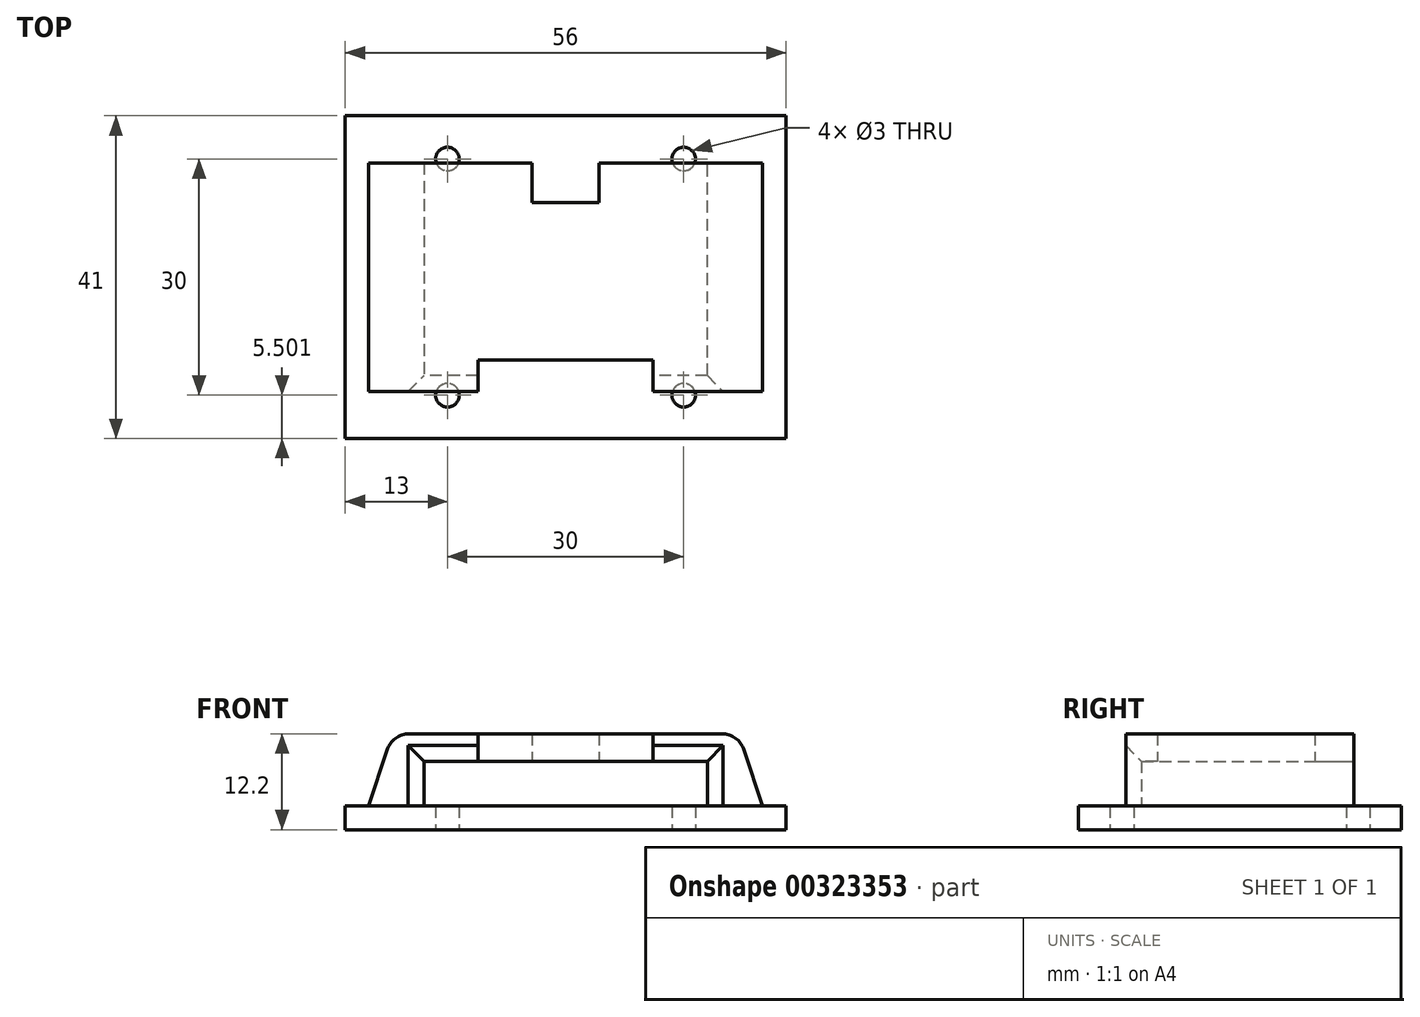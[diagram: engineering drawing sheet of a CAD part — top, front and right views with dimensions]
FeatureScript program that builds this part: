
annotation { "Feature Type Name" : "Feature", "Feature Type Description" : "" }
export const myFeature = defineFeature(function(context is Context, id is Id, definition is map)
    precondition{}
    {
        {
            var Q0;
            Q0=qCreatedBy(makeId("Top.planeOp"),FACE);
            var sketch = newSketch(context, id + "F0", { "sketchPlane" : qUnion([Q0])});
            skLineSegment(sketch, "E0", {"start": v(-18, 12.15) * mm, "end": v(-4.25, 12.15) * mm});
            skLineSegment(sketch, "E1", {"start": v(-4.25, 12.15) * mm, "end": v(-4.25, 7.15) * mm});
            skLineSegment(sketch, "E2", {"start": v(-4.25, 7.15) * mm, "end": v(4.25, 7.15) * mm});
            skLineSegment(sketch, "E3", {"start": v(4.25, 7.15) * mm, "end": v(4.25, 12.15) * mm});
            skLineSegment(sketch, "E4", {"start": v(4.25, 12.15) * mm, "end": v(18, 12.15) * mm});
            skLineSegment(sketch, "E5", {"start": v(18, 12.15) * mm, "end": v(18, -16.85) * mm});
            skLineSegment(sketch, "E6", {"start": v(18, -16.85) * mm, "end": v(11.12, -16.85) * mm});
            skLineSegment(sketch, "E7", {"start": v(11.12, -16.85) * mm, "end": v(11.12, -12.85) * mm});
            skLineSegment(sketch, "E8", {"start": v(11.12, -12.85) * mm, "end": v(-11.12, -12.85) * mm});
            skLineSegment(sketch, "E9", {"start": v(-11.12, -12.85) * mm, "end": v(-11.12, -16.85) * mm});
            skLineSegment(sketch, "E10", {"start": v(-11.12, -16.85) * mm, "end": v(-18, -16.85) * mm});
            skLineSegment(sketch, "E11", {"start": v(-18, -16.85) * mm, "end": v(-18, 12.15) * mm});
            skSolve(sketch);
        }
        {
            var Q0;
            Q0=qSketchRegion(id+"F0",true);
            extrude(context, id + "F1", {"entities" : qUnion([Q0]), "depth" : 3.5 * mm});
        }
        {
            var Q0;
            Q0=makeQuery(id+"F1.opExtrude","SWEPT_FACE",FACE,{"disambiguationData":[OSD([sQuery(id+"F0.wireOp",EDGE,"E11")])]});
            var sketch = newSketch(context, id + "F2", { "sketchPlane" : qUnion([Q0])});
            skLineSegment(sketch, "E12.bottom", {"start": v(-12.15, 3.5) * mm, "end": v(16.85, 3.5) * mm});
            skLineSegment(sketch, "E12.top", {"start": v(-12.15, -5.7) * mm, "end": v(16.85, -5.7) * mm});
            skLineSegment(sketch, "E12.left", {"start": v(-12.15, 3.5) * mm, "end": v(-12.15, -5.7) * mm});
            skLineSegment(sketch, "E12.right", {"start": v(16.85, 3.5) * mm, "end": v(16.85, -5.7) * mm});
            skSolve(sketch);
        }
        {
            var Q0;
            Q0=qSketchRegion(id+"F2",true);
            extrude(context, id + "F3", {"entities" : qUnion([Q0]), "operationType" : NewBodyOperationType.ADD, "depth" : 4 * mm});
        }
        {
            var Q0;
            Q0=makeQuery(id+"F1.opExtrude","SWEPT_FACE",FACE,{"disambiguationData":[OSD([sQuery(id+"F0.wireOp",EDGE,"E5")])]});
            var sketch = newSketch(context, id + "F4", { "sketchPlane" : qUnion([Q0])});
            skLineSegment(sketch, "E13.bottom", {"start": v(-16.85, 3.5) * mm, "end": v(12.15, 3.5) * mm});
            skLineSegment(sketch, "E13.top", {"start": v(-16.85, -5.7) * mm, "end": v(12.15, -5.7) * mm});
            skLineSegment(sketch, "E13.left", {"start": v(-16.85, 3.5) * mm, "end": v(-16.85, -5.7) * mm});
            skLineSegment(sketch, "E13.right", {"start": v(12.15, 3.5) * mm, "end": v(12.15, -5.7) * mm});
            skSolve(sketch);
        }
        {
            var Q0;
            Q0=qSketchRegion(id+"F4",true);
            extrude(context, id + "F5", {"entities" : qUnion([Q0]), "operationType" : NewBodyOperationType.ADD, "depth" : 4 * mm});
        }
        {
            var Q0;
            Q0=makeQuery(id+"F1.opExtrude","CAP_EDGE",EDGE,{"disambiguationData":[OSD([sQuery(id+"F0.wireOp",EDGE,"E10")])],"isStart":true});
            var Q1;
            Q1=makeQuery(id+"F1.opExtrude","CAP_EDGE",EDGE,{"disambiguationData":[OSD([sQuery(id+"F0.wireOp",EDGE,"E6")])],"isStart":true});
            chamfer(context, id + "F6", {"entities" : qUnion([Q0, Q1]), "width" : 2 * mm, "tangentPropagation" : true});
        }
        {
            var Q0;
            Q0=makeQuery(id+"F5.opExtrude","SWEPT_FACE",FACE,{"disambiguationData":[OSD([sQuery(id+"F4.wireOp",EDGE,"E13.top")])]});
            var sketch = newSketch(context, id + "F7", { "sketchPlane" : qUnion([Q0])});
            skLineSegment(sketch, "E14.bottom", {"start": v(22, -5.15) * mm, "end": v(18, -5.15) * mm});
            skLineSegment(sketch, "E14.top", {"start": v(22, 9.85) * mm, "end": v(18, 9.85) * mm});
            skLineSegment(sketch, "E14.left", {"start": v(22, -5.15) * mm, "end": v(22, 9.85) * mm});
            skLineSegment(sketch, "E14.right", {"start": v(18, -5.15) * mm, "end": v(18, 9.85) * mm});
            skLineSegment(sketch, "E15", {"start": v(41.9, 2.35) * mm, "end": v(-44.93, 2.35) * mm, "construction": true});
            skLineSegment(sketch, "E16.bottom", {"start": v(-22, -5.15) * mm, "end": v(-18, -5.15) * mm});
            skLineSegment(sketch, "E16.top", {"start": v(-22, 9.85) * mm, "end": v(-18, 9.85) * mm});
            skLineSegment(sketch, "E16.left", {"start": v(-22, -5.15) * mm, "end": v(-22, 9.85) * mm});
            skLineSegment(sketch, "E16.right", {"start": v(-18, -5.15) * mm, "end": v(-18, 9.85) * mm});
            skSolve(sketch);
        }
        {
            var Q0;
            Q0=qSketchRegion(id+"F7",true);
            extrude(context, id + "F8", {"entities" : qUnion([Q0]), "operationType" : NewBodyOperationType.ADD, "depth" : 3 * mm});
        }
        {
            var Q0;
            Q0=makeQuery(id+"F5.opExtrude","CAP_EDGE",EDGE,{"disambiguationData":[OSD([sQuery(id+"F4.wireOp",EDGE,"E13.left")])],"isStart":true});
            var Q1;
            Q1=makeQuery(id+"F3.opExtrude","CAP_EDGE",EDGE,{"disambiguationData":[OSD([sQuery(id+"F2.wireOp",EDGE,"E12.right")])],"isStart":true});
            chamfer(context, id + "F9", {"entities" : qUnion([Q0, Q1]), "width" : 2 * mm, "tangentPropagation" : true});
        }
        {
            var Q0;
            Q0=makeQuery(id+"F3.boolean.opBoolean","MERGE",FACE,{"derivedFrom":[makeQuery(id+"F1.opExtrude","SWEPT_FACE",FACE,{"disambiguationData":[OSD([sQuery(id+"F0.wireOp",EDGE,"E0")])]}),makeQuery(id+"F3.opExtrude","SWEPT_FACE",FACE,{"disambiguationData":[OSD([sQuery(id+"F2.wireOp",EDGE,"E12.left")])]})]});
            var sketch = newSketch(context, id + "F10", { "sketchPlane" : qUnion([Q0])});
            skLineSegment(sketch, "E17", {"start": v(22, 3.5) * mm, "end": v(22, -5.7) * mm});
            skLineSegment(sketch, "E18", {"start": v(22, -5.7) * mm, "end": v(25, -5.7) * mm});
            skLineSegment(sketch, "E19", {"start": v(25, -5.7) * mm, "end": v(22, 3.5) * mm});
            skLineSegment(sketch, "E20", {"start": v(0, 10.19) * mm, "end": v(0, -17.52) * mm, "construction": true});
            skLineSegment(sketch, "E21.MirrorCS", {"start": v(-22, 3.5) * mm, "end": v(-22, -5.7) * mm});
            skLineSegment(sketch, "E22.MirrorCS", {"start": v(-22, -5.7) * mm, "end": v(-25, -5.7) * mm});
            skLineSegment(sketch, "E23.MirrorCS", {"start": v(-25, -5.7) * mm, "end": v(-22, 3.5) * mm});
            skSolve(sketch);
        }
        {
            var Q0;
            Q0=qSketchRegion(id+"F10",true);
            var Q1;
            Q1=makeQuery(id+"F3.boolean.opBoolean","MERGE",FACE,{"derivedFrom":[makeQuery(id+"F1.opExtrude","SWEPT_FACE",FACE,{"disambiguationData":[OSD([sQuery(id+"F0.wireOp",EDGE,"E10")])]}),makeQuery(id+"F3.opExtrude","SWEPT_FACE",FACE,{"disambiguationData":[OSD([sQuery(id+"F2.wireOp",EDGE,"E12.right")])]})]});
            extrude(context, id + "F11", {"entities" : qUnion([Q0]), "operationType" : NewBodyOperationType.ADD, "endBound" : BoundingType.UP_TO_SURFACE, "oppositeDirection" : true, "endBoundEntityFace" : qUnion([Q1]), "depth" : 25 * mm});
        }
        {
            var Q0;
            {var subQ0=sQuery(id+"F2.wireOp",EDGE,"E12.bottom");Q0=makeQuery(id+"F11.boolean.opBoolean","MERGE",EDGE,{"derivedFrom":[makeQuery(id+"F3.opExtrude","CAP_EDGE",EDGE,{"disambiguationData":[OSD([subQ0])],"isStart":false}),makeQuery(id+"F11.opExtrude","SWEPT_EDGE",EDGE,{"disambiguationData":[OSD([sQuery(id+"F0.wireOp",EDGE,"E0"),subQ0,sQuery(id+"F2.wireOp",EDGE,"E12.left"),sQuery(id+"F10.wireOp",EDGE,"E17"),sQuery(id+"F10.wireOp",EDGE,"E19")])]})]});}
            var Q1;
            Q1=makeQuery(id+"F11.boolean.opBoolean","MERGE",EDGE,{"derivedFrom":[makeQuery(id+"F5.opExtrude","CAP_EDGE",EDGE,{"disambiguationData":[OSD([sQuery(id+"F4.wireOp",EDGE,"E13.bottom")])],"isStart":false}),makeQuery(id+"F11.opExtrude","SWEPT_EDGE",EDGE,{"disambiguationData":[OSD([sQuery(id+"F10.wireOp",EDGE,"E21.MirrorCS"),sQuery(id+"F10.wireOp",EDGE,"E23.MirrorCS")])]})]});
            fillet(context, id + "F12", {"entities" : qUnion([Q0, Q1]), "radius" : 3 * mm, "tangentPropagation" : true, "allowEdgeOverflow" : false});
        }
        {
            var Q0;
            {var subQ2=sQuery(id+"F4.wireOp",EDGE,"E13.top");var subQ8=makeQuery(id+"F5.opExtrude","SWEPT_FACE",FACE,{"disambiguationData":[OSD([subQ2])]});Q0=makeQuery(id+"F11.boolean.opBoolean","MERGE",FACE,{"derivedFrom":[makeQuery(id+"F8.boolean.opBoolean","SPLIT",FACE,{"disambiguationData":[TD([makeQuery(id+"F1.opExtrude","SWEPT_FACE",FACE,{"disambiguationData":[OSD([sQuery(id+"F0.wireOp",EDGE,"E4")])]})])],"derivedFrom":subQ8}),makeQuery(id+"F8.boolean.opBoolean","SPLIT",FACE,{"disambiguationData":[TD([makeQuery(id+"F1.opExtrude","SWEPT_FACE",FACE,{"disambiguationData":[OSD([sQuery(id+"F0.wireOp",EDGE,"E6")])]})])],"derivedFrom":subQ8}),makeQuery(id+"F11.opExtrude","SWEPT_FACE",FACE,{"disambiguationData":[OSD([sQuery(id+"F10.wireOp",EDGE,"E22.MirrorCS")])]})]});}
            var sketch = newSketch(context, id + "F13", { "sketchPlane" : qUnion([Q0])});
            skLineSegment(sketch, "E24.bottom", {"start": v(-28, 22.85) * mm, "end": v(28, 22.85) * mm});
            skLineSegment(sketch, "E24.top", {"start": v(-28, -18.15) * mm, "end": v(28, -18.15) * mm});
            skLineSegment(sketch, "E24.left", {"start": v(-28, 22.85) * mm, "end": v(-28, -18.15) * mm});
            skLineSegment(sketch, "E24.right", {"start": v(28, 22.85) * mm, "end": v(28, -18.15) * mm});
            skSolve(sketch);
        }
        {
            var Q0;
            Q0 = qSketchRegion(id + "F13", true);
            var Q1;
            Q1=makeQuery(id+"F8.opExtrude","CAP_FACE",FACE,{"disambiguationData":[OSD([sQuery(id+"F7.wireOp",EDGE,"E16.bottom"),sQuery(id+"F7.wireOp",EDGE,"E16.top"),sQuery(id+"F7.wireOp",EDGE,"E16.left"),sQuery(id+"F7.wireOp",EDGE,"E16.right")])],"isStart":false});
            extrude(context, id + "F14", {"entities" : qUnion([Q0]), "operationType" : NewBodyOperationType.ADD, "endBound" : BoundingType.UP_TO_SURFACE, "depth" : 25 * mm, "endBoundEntityFace" : qUnion([Q1]), "offsetDistance" : 25 * mm});
        }
        {
            var Q0;
            {var subQ0=sQuery(id+"F7.wireOp",EDGE,"E16.right");var subQ1=sQuery(id+"F7.wireOp",EDGE,"E16.left");var subQ2=sQuery(id+"F7.wireOp",EDGE,"E16.top");var subQ3=sQuery(id+"F7.wireOp",EDGE,"E16.bottom");Q0=makeQuery(id+"F14.boolean.opBoolean","MERGE",FACE,{"derivedFrom":[makeQuery(id+"F8.opExtrude","CAP_FACE",FACE,{"disambiguationData":[OSD([sQuery(id+"F7.wireOp",EDGE,"E14.bottom"),sQuery(id+"F7.wireOp",EDGE,"E14.top"),sQuery(id+"F7.wireOp",EDGE,"E14.left"),sQuery(id+"F7.wireOp",EDGE,"E14.right")])],"isStart":false}),makeQuery(id+"F8.opExtrude","CAP_FACE",FACE,{"disambiguationData":[OSD([subQ3,subQ2,subQ1,subQ0])],"isStart":false}),makeQuery(id+"F14.opExtrude","CAP_FACE",FACE,{"disambiguationData":[OSD([subQ3,subQ2,subQ1,subQ0])],"isStart":false})]});}
            var sketch = newSketch(context, id + "F15", { "sketchPlane" : qUnion([Q0])});
            skLineSegment(sketch, "E25", {"start": v(0, 8.2) * mm, "end": v(0, -6.72) * mm, "construction": true});
            skLineSegment(sketch, "E26", {"start": v(-10.77, 2.35) * mm, "end": v(9.05, 2.35) * mm, "construction": true});
            skCircle(sketch, "E27", {"center": v(-15, 17.35) * mm, "radius": 1.5 * mm});
            skCircle(sketch, "E28.MirrorC", {"center": v(15, 17.35) * mm, "radius": 1.5 * mm});
            skLineSegment(sketch, "E29.MirrorCS", {"start": v(0, -3.5) * mm, "end": v(0, 11.42) * mm, "construction": true});
            skCircle(sketch, "E30.MirrorC", {"center": v(15, -12.65) * mm, "radius": 1.5 * mm});
            skCircle(sketch, "E31.MirrorC", {"center": v(-15, -12.65) * mm, "radius": 1.5 * mm});
            skSolve(sketch);
        }
        {
            var Q0;
            Q0 = qSketchRegion(id + "F15", true);
            extrude(context, id + "F16", {"entities" : qUnion([Q0]), "operationType" : NewBodyOperationType.REMOVE, "endBound" : BoundingType.UP_TO_NEXT, "oppositeDirection" : true, "depth" : 25 * mm, "offsetDistance" : 25 * mm});
        }
    });
